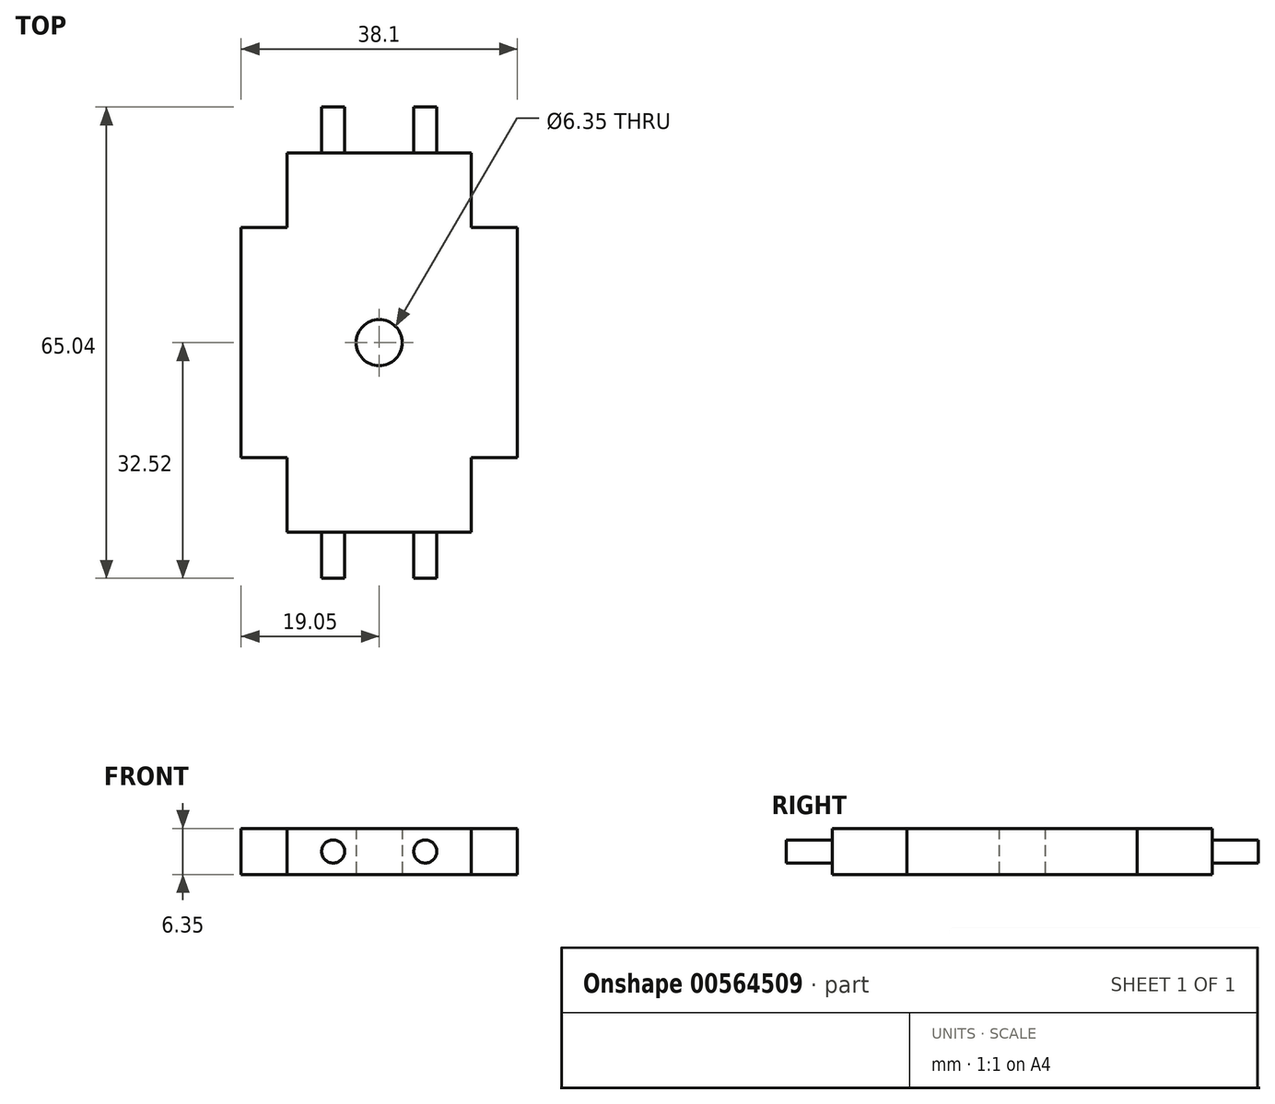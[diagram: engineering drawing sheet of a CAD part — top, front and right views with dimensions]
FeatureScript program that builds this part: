
annotation { "Feature Type Name" : "Feature", "Feature Type Description" : "" }
export const myFeature = defineFeature(function(context is Context, id is Id, definition is map)
    precondition{}
    {
        {
            var Q0;
            Q0=qCreatedBy(makeId("Top.planeOp"),FACE);
            var sketch = newSketch(context, id + "F0", { "sketchPlane" : qUnion([Q0])});
            skLineSegment(sketch, "E0.bottom", {"start": v(12.7, 26.17) * mm, "end": v(-12.7, 26.17) * mm});
            skLineSegment(sketch, "E0.top", {"start": v(12.7, -26.17) * mm, "end": v(-12.7, -26.17) * mm});
            skLineSegment(sketch, "E0.left", {"start": v(12.7, 26.17) * mm, "end": v(12.7, 15.88) * mm});
            skLineSegment(sketch, "E0.right", {"start": v(-12.7, 26.17) * mm, "end": v(-12.7, 15.87) * mm});
            skPoint(sketch, "E0.middle", {"position": v(0, 0) * mm});
            skLineSegment(sketch, "E1.bottom", {"start": v(19.05, 15.88) * mm, "end": v(12.7, 15.88) * mm});
            skLineSegment(sketch, "E1.top", {"start": v(19.05, -15.87) * mm, "end": v(12.7, -15.88) * mm});
            skLineSegment(sketch, "E1.left", {"start": v(19.05, 15.88) * mm, "end": v(19.05, -15.87) * mm});
            skLineSegment(sketch, "E1.right", {"start": v(-19.05, 15.87) * mm, "end": v(-19.05, -15.88) * mm});
            skLineSegment(sketch, "E2.trimOffspring", {"start": v(-12.7, 15.88) * mm, "end": v(-19.05, 15.88) * mm});
            skLineSegment(sketch, "E3.trimOffspring", {"start": v(12.7, -15.88) * mm, "end": v(12.7, -26.17) * mm});
            skLineSegment(sketch, "E4.trimOffspring", {"start": v(-12.7, -15.88) * mm, "end": v(-19.05, -15.88) * mm});
            skLineSegment(sketch, "E5.trimOffspring", {"start": v(-12.7, -15.88) * mm, "end": v(-12.7, -26.17) * mm});
            skCircle(sketch, "E6", {"center": v(0, 0) * mm, "radius": 3.18 * mm});
            skSolve(sketch);
        }
        {
            var Q0;
            Q0=makeQuery(id+"F0.imprint","IMPRINT",FACE,{"disambiguationData":[TD([[makeQuery(id+"F0.imprint","IMPRINT",EDGE,{"derivedFrom":sQuery(id+"F0.wireOp",EDGE,"E0.bottom")}),1.0]])]});
            extrude(context, id + "F1", {"entities" : qUnion([Q0]), "depth" : 6.35 * mm, "offsetDistance" : 25.4 * mm});
        }
        {
            var Q0;
            Q0=makeQuery(id+"F1.opExtrude","SWEPT_FACE",FACE,{"disambiguationData":[OSD([sQuery(id+"F0.wireOp",EDGE,"E0.bottom")])]});
            var sketch = newSketch(context, id + "F2", { "sketchPlane" : qUnion([Q0])});
            skCircle(sketch, "E7", {"center": v(6.35, 3.18) * mm, "radius": 1.59 * mm});
            skCircle(sketch, "E8", {"center": v(-6.35, 3.18) * mm, "radius": 1.59 * mm});
            skSolve(sketch);
        }
        {
            var Q0;
            Q0=makeQuery(id+"F2.imprint","IMPRINT",FACE,{"disambiguationData":[TD([[makeQuery(id+"F2.imprint","IMPRINT",EDGE,{"derivedFrom":sQuery(id+"F2.wireOp",EDGE,"E8")}),1.0]])]});
            extrude(context, id + "F3", {"entities" : qUnion([Q0]), "operationType" : NewBodyOperationType.ADD, "depth" : 6.35 * mm, "offsetDistance" : 25.4 * mm});
        }
        {
            var Q0;
            Q0=makeQuery(id+"F2.imprint","IMPRINT",FACE,{"disambiguationData":[TD([[makeQuery(id+"F2.imprint","IMPRINT",EDGE,{"derivedFrom":sQuery(id+"F2.wireOp",EDGE,"E7")}),1.0]])]});
            extrude(context, id + "F4", {"entities" : qUnion([Q0]), "operationType" : NewBodyOperationType.ADD, "depth" : 6.35 * mm, "offsetDistance" : 25.4 * mm});
        }
        {
            var Q0;
            Q0=makeQuery(id+"F1.opExtrude","SWEPT_FACE",FACE,{"disambiguationData":[OSD([sQuery(id+"F0.wireOp",EDGE,"E0.top")])]});
            var sketch = newSketch(context, id + "F5", { "sketchPlane" : qUnion([Q0])});
            skCircle(sketch, "E9", {"center": v(-6.35, 3.18) * mm, "radius": 1.59 * mm});
            skCircle(sketch, "E10", {"center": v(6.35, 3.18) * mm, "radius": 1.59 * mm});
            skSolve(sketch);
        }
        {
            var Q0;
            Q0=makeQuery(id+"F5.imprint","IMPRINT",FACE,{"disambiguationData":[TD([[makeQuery(id+"F5.imprint","IMPRINT",EDGE,{"derivedFrom":sQuery(id+"F5.wireOp",EDGE,"E9")}),1.0]])]});
            extrude(context, id + "F6", {"entities" : qUnion([Q0]), "operationType" : NewBodyOperationType.ADD, "depth" : 6.35 * mm, "offsetDistance" : 25.4 * mm});
        }
        {
            var Q0;
            Q0 = qSketchRegion(id + "F5", true);
            extrude(context, id + "F7", {"entities" : qUnion([Q0]), "operationType" : NewBodyOperationType.ADD, "depth" : 6.35 * mm, "offsetDistance" : 25.4 * mm});
        }
    });
